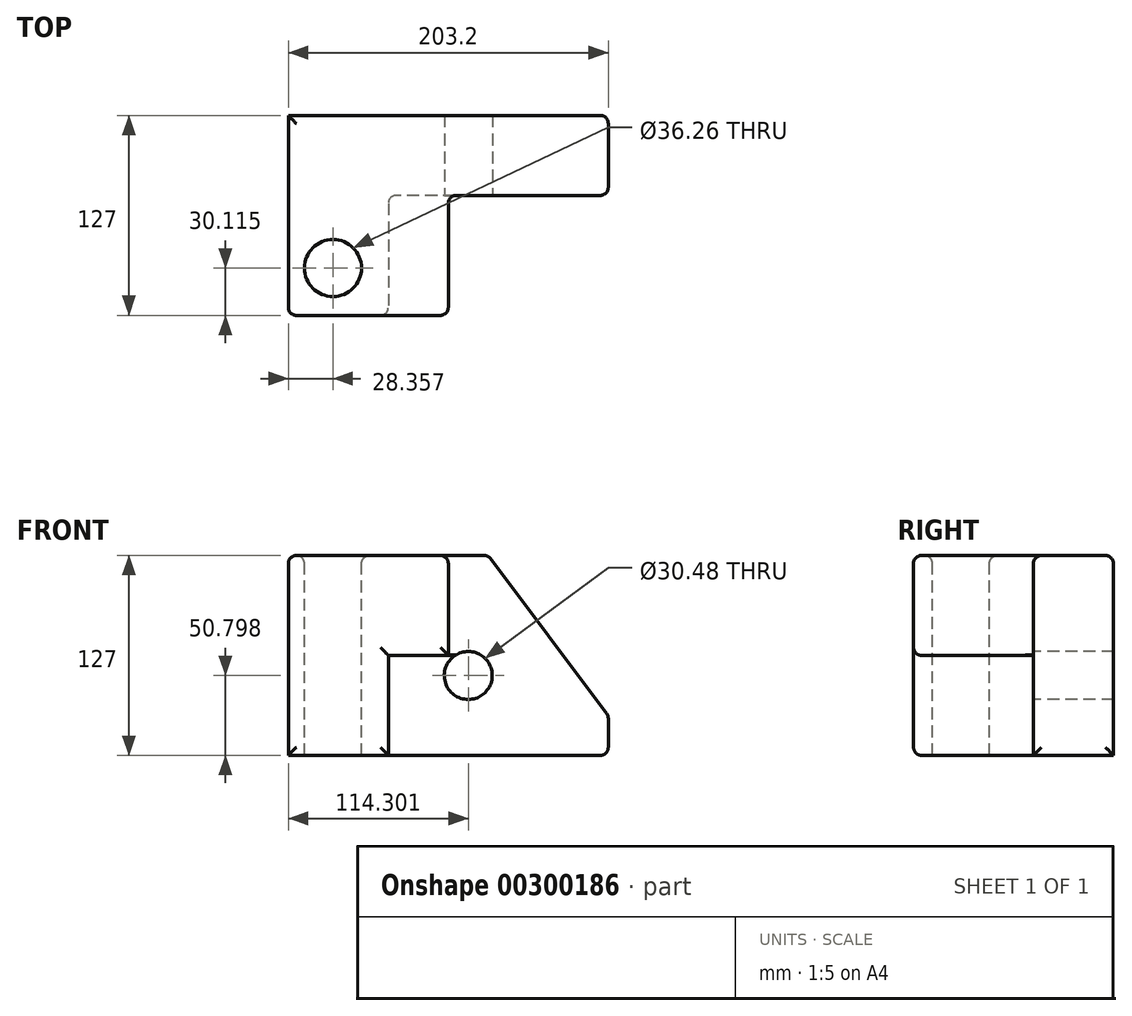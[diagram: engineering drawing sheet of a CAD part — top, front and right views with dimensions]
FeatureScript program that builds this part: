
annotation { "Feature Type Name" : "Feature", "Feature Type Description" : "" }
export const myFeature = defineFeature(function(context is Context, id is Id, definition is map)
    precondition{}
    {
        {
            var Q0;
            Q0=qCreatedBy(makeId("Front.planeOp"),FACE);
            var sketch = newSketch(context, id + "F0", { "sketchPlane" : qUnion([Q0])});
            skLineSegment(sketch, "E0.bottom", {"start": v(71.6, -51.83) * mm, "end": v(-131.6, -51.83) * mm});
            skLineSegment(sketch, "E0.top", {"start": v(71.6, 75.17) * mm, "end": v(-131.6, 75.17) * mm});
            skLineSegment(sketch, "E0.left", {"start": v(71.6, -51.83) * mm, "end": v(71.6, 75.17) * mm});
            skLineSegment(sketch, "E0.right", {"start": v(-131.6, -51.83) * mm, "end": v(-131.6, 75.17) * mm});
            skPoint(sketch, "E0.middle", {"position": v(-30, 11.67) * mm});
            skSolve(sketch);
        }
        {
            var Q0;
            Q0=makeQuery(id+"F0.imprint","IMPRINT",FACE,{"disambiguationData":[TD([[makeQuery(id+"F0.imprint","IMPRINT",EDGE,{"derivedFrom":sQuery(id+"F0.wireOp",EDGE,"E0.bottom")}),-1.0]])]});
            extrude(context, id + "F1", {"entities" : qUnion([Q0]), "depth" : 127 * mm});
        }
        {
            var Q0;
            Q0=makeQuery(id+"F1.opExtrude","CAP_FACE",FACE,{"disambiguationData":[OSD([sQuery(id+"F0.wireOp",EDGE,"E0.bottom"),sQuery(id+"F0.wireOp",EDGE,"E0.top"),sQuery(id+"F0.wireOp",EDGE,"E0.left"),sQuery(id+"F0.wireOp",EDGE,"E0.right")])],"isStart":false});
            var sketch = newSketch(context, id + "F2", { "sketchPlane" : qUnion([Q0])});
            skLineSegment(sketch, "E1", {"start": v(-131.6, -51.83) * mm, "end": v(-131.6, 75.17) * mm});
            skLineSegment(sketch, "E2", {"start": v(-131.6, 75.17) * mm, "end": v(-30, 75.17) * mm});
            skLineSegment(sketch, "E3", {"start": v(-30, 75.17) * mm, "end": v(-30, 11.67) * mm});
            skLineSegment(sketch, "E4", {"start": v(-30, 11.67) * mm, "end": v(-68.1, 11.67) * mm});
            skLineSegment(sketch, "E5", {"start": v(-68.1, 11.67) * mm, "end": v(-68.1, -51.83) * mm});
            skLineSegment(sketch, "E6", {"start": v(-68.1, -51.83) * mm, "end": v(-131.6, -51.83) * mm});
            skSolve(sketch);
        }
        {
            var Q0;
            {var subQ3=sQuery(id+"F2.wireOp",EDGE,"E3");Q0=makeQuery(id+"F2.imprint","IMPRINT",FACE,{"disambiguationData":[TD([[makeQuery(id+"F2.imprint","IMPRINT",EDGE,{"derivedFrom":subQ3}),1.0]])]});}
            extrude(context, id + "F3", {"entities" : qUnion([Q0]), "operationType" : NewBodyOperationType.REMOVE, "oppositeDirection" : true, "depth" : 76.2 * mm});
        }
        {
            var Q0;
            Q0=makeQuery(id+"F1.opExtrude","SWEPT_EDGE",EDGE,{"disambiguationData":[OSD([sQuery(id+"F0.wireOp",EDGE,"E0.top"),sQuery(id+"F0.wireOp",EDGE,"E0.left")])]});
            chamfer(context, id + "F4", {"entities" : qUnion([Q0]), "chamferType" : ChamferType.TWO_OFFSETS, "width1" : 76.2 * mm, "oppositeDirection" : false, "width2" : 101.6 * mm, "tangentPropagation" : true});
        }
        {
            var Q0;
            Q0=makeQuery(id+"F3.boolean.opBoolean","COPY",FACE,{"derivedFrom":makeQuery(id+"F3.opExtrude","CAP_FACE",FACE,{"disambiguationData":[OSD([sQuery(id+"F0.wireOp",EDGE,"E0.bottom"),sQuery(id+"F0.wireOp",EDGE,"E0.top"),sQuery(id+"F0.wireOp",EDGE,"E0.left"),sQuery(id+"F2.wireOp",EDGE,"E3"),sQuery(id+"F2.wireOp",EDGE,"E4"),sQuery(id+"F2.wireOp",EDGE,"E5")])],"isStart":false})});
            var sketch = newSketch(context, id + "F5", { "sketchPlane" : qUnion([Q0])});
            skCircle(sketch, "E7", {"center": v(-17.3, -1.03) * mm, "radius": 15.24 * mm});
            skSolve(sketch);
        }
        {
            var Q0;
            Q0=makeQuery(id+"F5.imprint","IMPRINT",FACE,{"disambiguationData":[TD([[makeQuery(id+"F5.imprint","IMPRINT",EDGE,{"derivedFrom":sQuery(id+"F5.wireOp",EDGE,"E7")}),1.0]])]});
            var Q1;
            Q1=makeQuery(id+"F1.opExtrude","CAP_FACE",FACE,{"disambiguationData":[OSD([sQuery(id+"F0.wireOp",EDGE,"E0.bottom"),sQuery(id+"F0.wireOp",EDGE,"E0.top"),sQuery(id+"F0.wireOp",EDGE,"E0.left"),sQuery(id+"F0.wireOp",EDGE,"E0.right")])],"isStart":true});
            extrude(context, id + "F6", {"entities" : qUnion([Q0]), "operationType" : NewBodyOperationType.REMOVE, "endBound" : BoundingType.UP_TO_SURFACE, "oppositeDirection" : true, "endBoundEntityFace" : qUnion([Q1]), "depth" : 25.4 * mm});
        }
        {
            var Q0;
            Q0=makeQuery(id+"F1.opExtrude","SWEPT_FACE",FACE,{"disambiguationData":[OSD([sQuery(id+"F0.wireOp",EDGE,"E0.top")])]});
            var sketch = newSketch(context, id + "F7", { "sketchPlane" : qUnion([Q0])});
            skCircle(sketch, "E8", {"center": v(-103.25, -96.89) * mm, "radius": 18.13 * mm});
            skSolve(sketch);
        }
        {
            var Q0;
            Q0=makeQuery(id+"F7.imprint","IMPRINT",FACE,{"disambiguationData":[TD([[makeQuery(id+"F7.imprint","IMPRINT",EDGE,{"derivedFrom":sQuery(id+"F7.wireOp",EDGE,"E8")}),1.0]])]});
            var Q1;
            Q1=makeQuery(id+"F1.opExtrude","SWEPT_FACE",FACE,{"disambiguationData":[OSD([sQuery(id+"F0.wireOp",EDGE,"E0.bottom")])]});
            extrude(context, id + "F8", {"entities" : qUnion([Q0]), "operationType" : NewBodyOperationType.REMOVE, "endBound" : BoundingType.UP_TO_SURFACE, "oppositeDirection" : true, "endBoundEntityFace" : qUnion([Q1]), "depth" : 25.4 * mm});
        }
        {
            var Q0;
            Q0=makeQuery(id+"F1.opExtrude","CAP_EDGE",EDGE,{"disambiguationData":[OSD([sQuery(id+"F0.wireOp",EDGE,"E0.top")])],"isStart":false});
            var Q1;
            Q1=makeQuery(id+"F3.boolean.opBoolean","COPY",EDGE,{"derivedFrom":makeQuery(id+"F3.opExtrude","SWEPT_EDGE",EDGE,{"disambiguationData":[OSD([sQuery(id+"F0.wireOp",EDGE,"E0.top"),sQuery(id+"F2.wireOp",EDGE,"E2"),sQuery(id+"F2.wireOp",EDGE,"E3")])]})});
            var Q2;
            Q2=makeQuery(id+"F3.boolean.opBoolean","COPY",EDGE,{"derivedFrom":makeQuery(id+"F3.opExtrude","CAP_EDGE",EDGE,{"disambiguationData":[OSD([sQuery(id+"F2.wireOp",EDGE,"E3")])],"isStart":true})});
            var Q3;
            Q3=makeQuery(id+"F3.boolean.opBoolean","COPY",EDGE,{"derivedFrom":makeQuery(id+"F3.opExtrude","CAP_EDGE",EDGE,{"disambiguationData":[OSD([sQuery(id+"F2.wireOp",EDGE,"E3")])],"isStart":false})});
            var Q4;
            {var subQ0=sQuery(id+"F0.wireOp",EDGE,"E0.left");var subQ1=sQuery(id+"F0.wireOp",EDGE,"E0.top");Q4=makeQuery(id+"F4.opChamfer","BLEND_EDGE",EDGE,{"blendedFrom":[makeQuery(id+"F1.opExtrude","SWEPT_EDGE",EDGE,{"disambiguationData":[OSD([subQ1,subQ0])]}),makeQuery(id+"F3.boolean.opBoolean","COPY",FACE,{"derivedFrom":makeQuery(id+"F3.opExtrude","CAP_FACE",FACE,{"disambiguationData":[OSD([sQuery(id+"F0.wireOp",EDGE,"E0.bottom"),subQ1,subQ0,sQuery(id+"F2.wireOp",EDGE,"E3"),sQuery(id+"F2.wireOp",EDGE,"E4"),sQuery(id+"F2.wireOp",EDGE,"E5")])],"isStart":false})})],"blendedInto":[makeQuery(id+"F3.boolean.opBoolean","COPY",FACE,{"derivedFrom":makeQuery(id+"F3.opExtrude","CAP_FACE",FACE,{"disambiguationData":[OSD([sQuery(id+"F0.wireOp",EDGE,"E0.bottom"),subQ1,subQ0,sQuery(id+"F2.wireOp",EDGE,"E3"),sQuery(id+"F2.wireOp",EDGE,"E4"),sQuery(id+"F2.wireOp",EDGE,"E5")])],"isStart":false})})]});}
            var Q5;
            Q5=makeQuery(id+"F4.opChamfer","BLEND_FACE",FACE,{"disambiguationData":[OSD([sQuery(id+"F0.wireOp",EDGE,"E0.top"),sQuery(id+"F0.wireOp",EDGE,"E0.left")])]});
            var Q6;
            Q6=makeQuery(id+"F1.opExtrude","SWEPT_FACE",FACE,{"disambiguationData":[OSD([sQuery(id+"F0.wireOp",EDGE,"E0.left")])]});
            var Q7;
            Q7=makeQuery(id+"F3.boolean.opBoolean","COPY",EDGE,{"derivedFrom":makeQuery(id+"F3.opExtrude","CAP_EDGE",EDGE,{"disambiguationData":[OSD([sQuery(id+"F0.wireOp",EDGE,"E0.bottom")])],"isStart":false})});
            var Q8;
            Q8=makeQuery(id+"F3.boolean.opBoolean","COPY",EDGE,{"derivedFrom":makeQuery(id+"F3.opExtrude","CAP_EDGE",EDGE,{"disambiguationData":[OSD([sQuery(id+"F2.wireOp",EDGE,"E5")])],"isStart":false})});
            var Q9;
            Q9=makeQuery(id+"F3.boolean.opBoolean","COPY",EDGE,{"derivedFrom":makeQuery(id+"F3.opExtrude","SWEPT_EDGE",EDGE,{"disambiguationData":[OSD([sQuery(id+"F0.wireOp",EDGE,"E0.bottom"),sQuery(id+"F2.wireOp",EDGE,"E5"),sQuery(id+"F2.wireOp",EDGE,"E6")])]})});
            var Q10;
            Q10=makeQuery(id+"F1.opExtrude","CAP_FACE",FACE,{"disambiguationData":[OSD([sQuery(id+"F0.wireOp",EDGE,"E0.bottom"),sQuery(id+"F0.wireOp",EDGE,"E0.top"),sQuery(id+"F0.wireOp",EDGE,"E0.left"),sQuery(id+"F0.wireOp",EDGE,"E0.right")])],"isStart":false});
            var Q11;
            Q11=makeQuery(id+"F1.opExtrude","SWEPT_FACE",FACE,{"disambiguationData":[OSD([sQuery(id+"F0.wireOp",EDGE,"E0.top")])]});
            fillet(context, id + "F9", {"entities" : qUnion([Q0, Q1, Q2, Q3, Q4, Q5, Q6, Q7, Q8, Q9, Q10, Q11]), "radius" : 5.08 * mm, "tangentPropagation" : true, "allowEdgeOverflow" : false});
        }
    });
